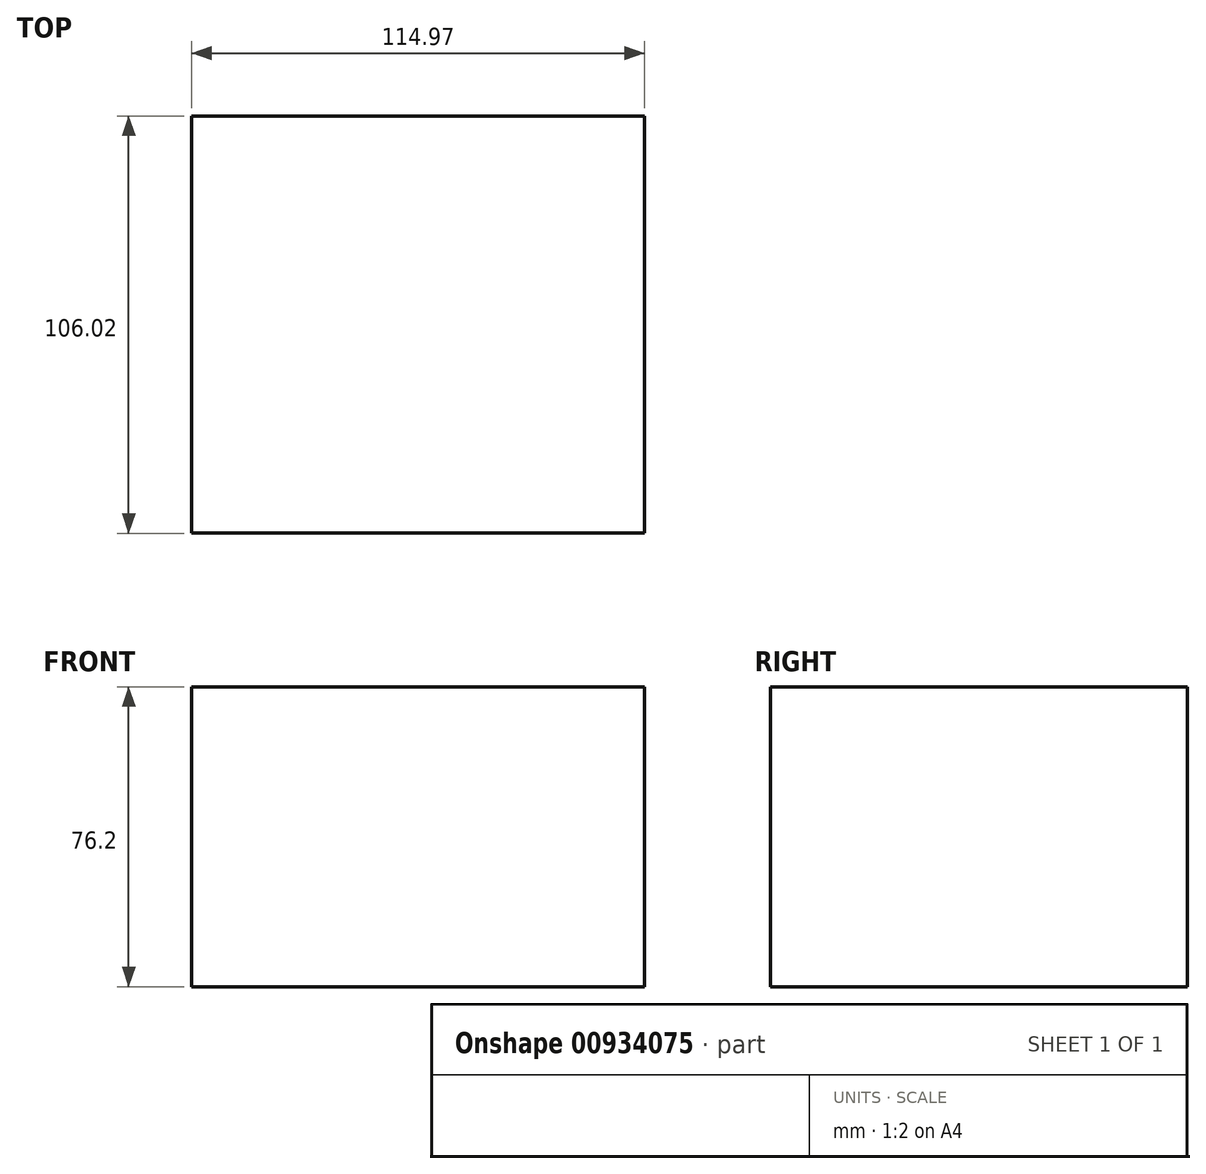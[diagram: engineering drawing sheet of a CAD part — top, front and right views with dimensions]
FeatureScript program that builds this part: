
annotation { "Feature Type Name" : "Feature", "Feature Type Description" : "" }
export const myFeature = defineFeature(function(context is Context, id is Id, definition is map)
    precondition{}
    {
        {
            var Q0;
            Q0=qCreatedBy(makeId("Top.planeOp"),FACE);
            var sketch = newSketch(context, id + "F0", { "sketchPlane" : qUnion([Q0])});
            skLineSegment(sketch, "E0.bottom", {"start": v(-58.1, 46.68) * mm, "end": v(56.87, 46.68) * mm});
            skLineSegment(sketch, "E0.top", {"start": v(-58.1, -59.34) * mm, "end": v(56.87, -59.34) * mm});
            skLineSegment(sketch, "E0.left", {"start": v(-58.1, 46.68) * mm, "end": v(-58.1, -59.34) * mm});
            skLineSegment(sketch, "E0.right", {"start": v(56.87, 46.68) * mm, "end": v(56.87, -59.34) * mm});
            skSolve(sketch);
        }
        {
            var Q0;
            Q0 = qSketchRegion(id + "F0", true);
            extrude(context, id + "F1", {"entities" : qUnion([Q0]), "depth" : 76.2 * mm, "offsetDistance" : 25.4 * mm});
        }
    });
